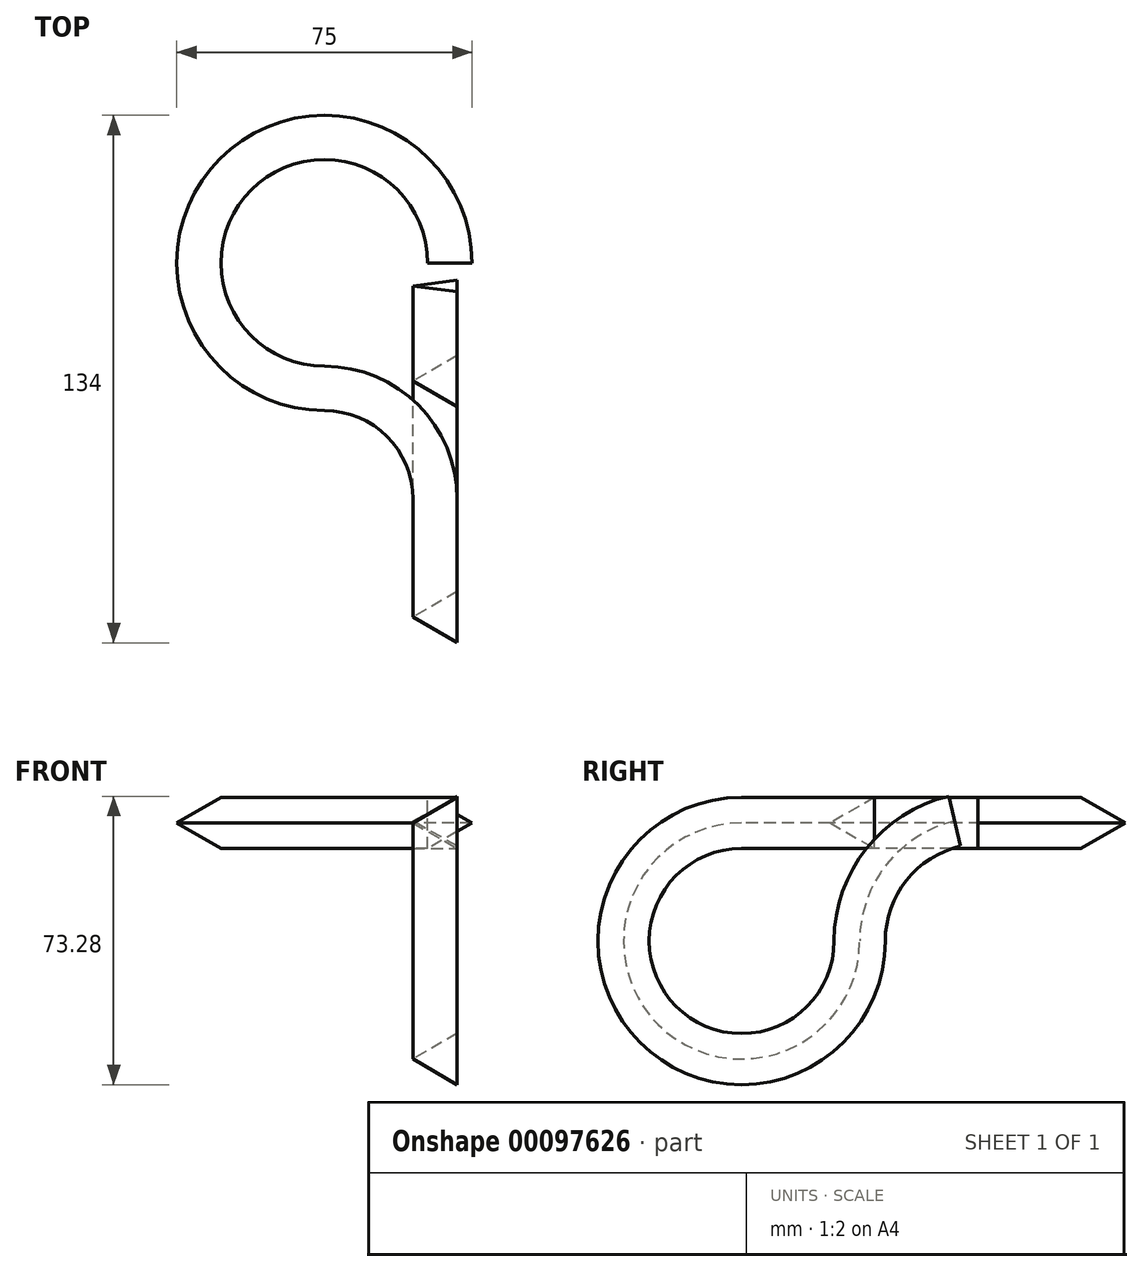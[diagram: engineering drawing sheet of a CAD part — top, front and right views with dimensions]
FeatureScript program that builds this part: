
annotation { "Feature Type Name" : "Feature", "Feature Type Description" : "" }
export const myFeature = defineFeature(function(context is Context, id is Id, definition is map)
    precondition{}
    {
        {
            var Q0;
            Q0=qCreatedBy(makeId("Top.planeOp"),FACE);
            var sketch = newSketch(context, id + "F0", { "sketchPlane" : qUnion([Q0])});
            skArc(sketch, "E0", {"start": v(-30, 0) * mm, "mid": v(-51.21, 51.21) * mm, "end": v(0, 30) * mm});
            skArc(sketch, "E1", {"start": v(0, -30) * mm, "mid": v(-8.79, -8.79) * mm, "end": v(-30, 0) * mm});
            skSolve(sketch);
        }
        {
            var Q0;
            Q0=qCreatedBy(makeId("Front.planeOp"),FACE);
            cPlane(context, id + "F1", {"entities" : qUnion([Q0]), "cplaneType" : CPlaneType.OFFSET, "offset" : 30 * mm, "oppositeDirection" : true, "width" : 150 * mm, "height" : 150 * mm});
        }
        {
            var Q0;
            Q0=qCreatedBy(id+"F1.planeOp",FACE);
            var sketch = newSketch(context, id + "F5", { "sketchPlane" : qUnion([Q0])});
            skCircle(sketch, "E2.cCircle", {"center": v(0, 0) * mm, "radius": 7.5 * mm, "construction": true});
            skLineSegment(sketch, "E2.0", {"start": v(7.5, 0) * mm, "end": v(-3.75, -6.5) * mm});
            skLineSegment(sketch, "E2.1", {"start": v(-3.75, -6.5) * mm, "end": v(-3.75, 6.5) * mm});
            skLineSegment(sketch, "E2.2", {"start": v(-3.75, 6.5) * mm, "end": v(7.5, 0) * mm});
            skSolve(sketch);
        }
        {
            var Q0;
            Q0=qCreatedBy(makeId("Top.planeOp"),FACE);
            var sketch = newSketch(context, id + "F2", { "sketchPlane" : qUnion([Q0])});
            skLineSegment(sketch, "E3", {"start": v(0, 0) * mm, "end": v(0, 16.06) * mm, "construction": true});
            skSolve(sketch);
        }
        {
            var Q0;
            Q0=sQuery(id+"F2.wireOp",EDGE,"E3");
            var Q1;
            Q1=qCreatedBy(makeId("Top.planeOp"),FACE);
            cPlane(context, id + "F3", {"entities" : qUnion([Q0, Q1]), "cplaneType" : CPlaneType.LINE_ANGLE, "offset" : 25 * mm, "angle" : 90 * degree, "width" : 150 * mm, "height" : 150 * mm});
        }
        {
            var Q0;
            Q0=qCreatedBy(id+"F3.planeOp",FACE);
            var sketch = newSketch(context, id + "F6", { "sketchPlane" : qUnion([Q0])});
            skArc(sketch, "E4", {"start": v(0, -30) * mm, "mid": v(-6.77, -10.56) * mm, "end": v(-24.16, 0.46) * mm});
            skArc(sketch, "E5", {"start": v(0, -30) * mm, "mid": v(51.21, -51.21) * mm, "end": v(30, 0) * mm});
            skSolve(sketch);
        }
        {
            var Q0;
            Q0=makeQuery(id+"F5.imprint","IMPRINT",FACE,{"disambiguationData":[TD([[makeQuery(id+"F5.imprint","IMPRINT",EDGE,{"derivedFrom":sQuery(id+"F5.wireOp",EDGE,"E2.0")}),-1.0]])]});
            var Q1;
            Q1=sQuery(id+"F0.wireOp",EDGE,"E0");
            var Q2;
            Q2=sQuery(id+"F0.wireOp",EDGE,"E1");
            var Q3;
            Q3=sQuery(id+"F6.wireOp",EDGE,"E5");
            var Q4;
            Q4=sQuery(id+"F6.wireOp",EDGE,"E4");
            sweep(context, id + "F4", {"profiles" : qUnion([Q0]), "path" : qUnion([Q1, Q2, Q3, Q4])});
        }
    });
